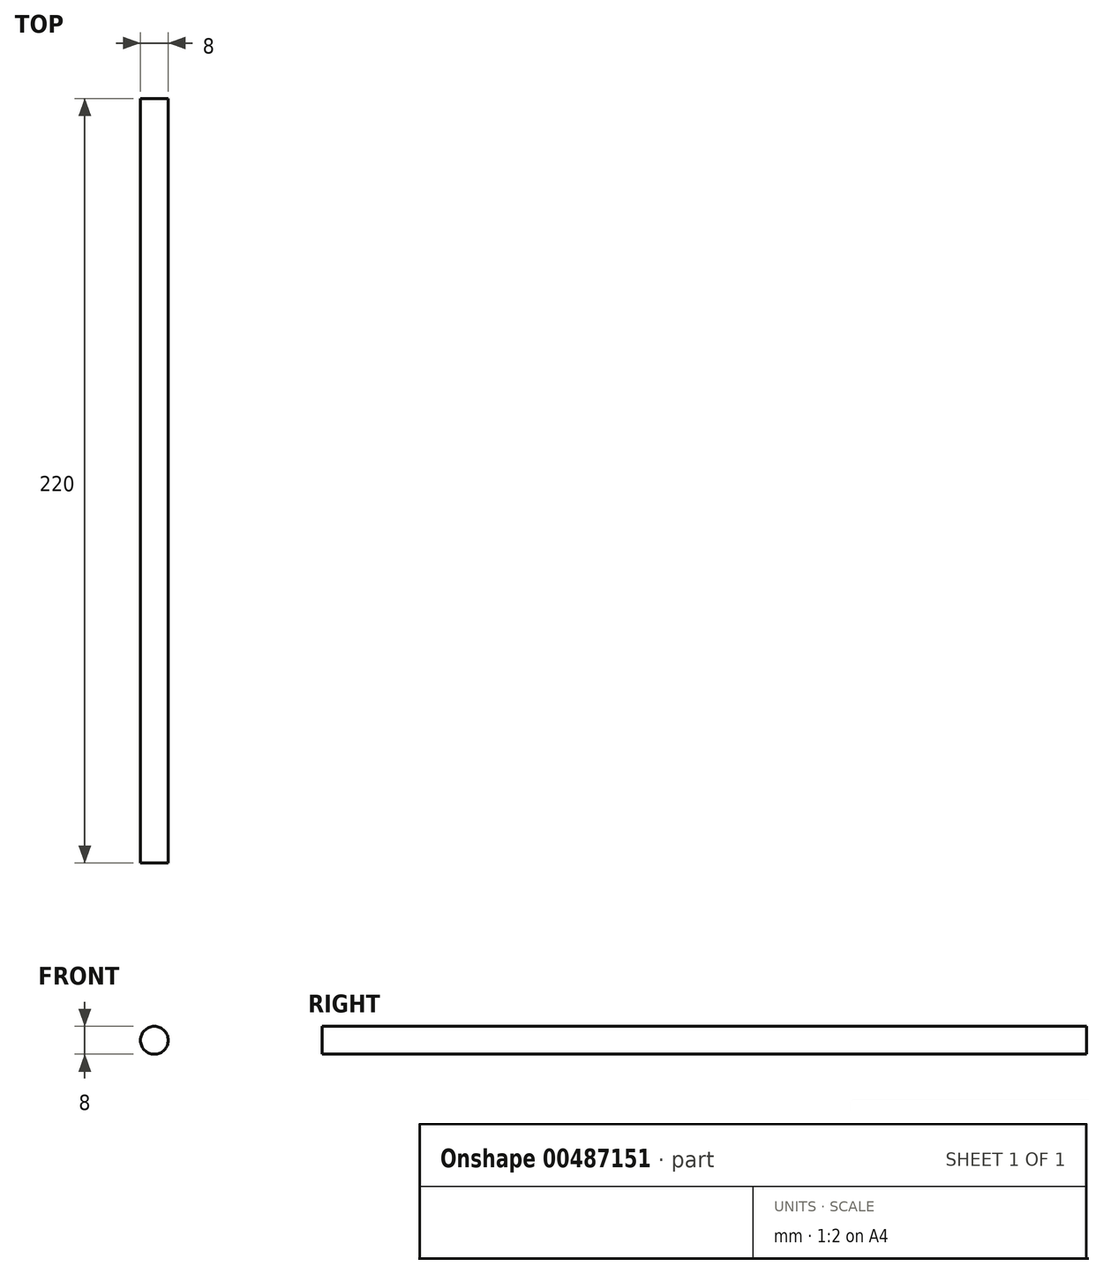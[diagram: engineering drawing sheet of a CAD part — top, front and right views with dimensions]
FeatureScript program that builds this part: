
annotation { "Feature Type Name" : "Feature", "Feature Type Description" : "" }
export const myFeature = defineFeature(function(context is Context, id is Id, definition is map)
    precondition{}
    {
        {
            var Q0;
            Q0=qCreatedBy(makeId("Front.planeOp"),FACE);
            var sketch = newSketch(context, id + "F0", { "sketchPlane" : qUnion([Q0])});
            skCircle(sketch, "E0", {"center": v(0, 0) * mm, "radius": 4 * mm});
            skSolve(sketch);
        }
        {
            var Q0;
            Q0 = qSketchRegion(id + "F0", true);
            extrude(context, id + "F1", {"entities" : qUnion([Q0]), "depth" : 110 * mm, "hasSecondDirection" : true, "secondDirectionOppositeDirection" : true, "secondDirectionDepth" : 110 * mm});
        }
    });
